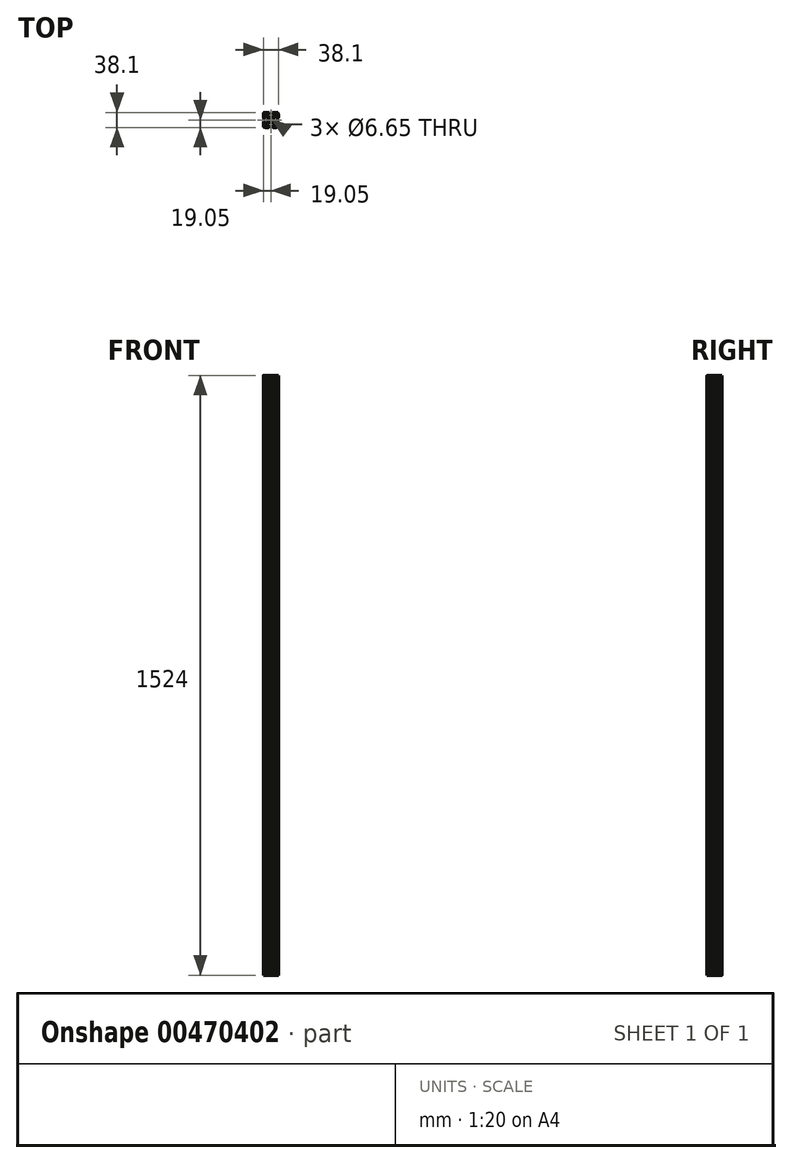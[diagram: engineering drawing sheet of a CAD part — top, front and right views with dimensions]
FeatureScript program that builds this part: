
annotation { "Feature Type Name" : "Feature", "Feature Type Description" : "" }
export const myFeature = defineFeature(function(context is Context, id is Id, definition is map)
    precondition{}
    {
        {
            var Q0;
            Q0=qCreatedBy(makeId("Top.planeOp"),FACE);
            var sketch = newSketch(context, id + "F0", { "sketchPlane" : qUnion([Q0])});
            skCircle(sketch, "E0", {"center": v(0, 0) * mm, "radius": 3.33 * mm});
            skArc(sketch, "E1", {"start": v(-10.29, 13.55) * mm, "mid": v(-10.22, 13.2) * mm, "end": v(-10.02, 12.91) * mm});
            skLineSegment(sketch, "E2", {"start": v(-10.29, 13.55) * mm, "end": v(-10.29, 14.08) * mm});
            skArc(sketch, "E3", {"start": v(-9.39, 14.99) * mm, "mid": v(-10.02, 14.72) * mm, "end": v(-10.29, 14.08) * mm});
            skLineSegment(sketch, "E4", {"start": v(-9.39, 14.99) * mm, "end": v(-5.62, 14.99) * mm});
            skArc(sketch, "E5", {"start": v(-5.62, 14.99) * mm, "mid": v(-4.52, 15.44) * mm, "end": v(-4.06, 16.54) * mm});
            skLineSegment(sketch, "E6", {"start": v(-4.06, 16.54) * mm, "end": v(-4.06, 17.5) * mm});
            skArc(sketch, "E7", {"start": v(-4.06, 17.5) * mm, "mid": v(-4.52, 18.6) * mm, "end": v(-5.62, 19.05) * mm});
            skLineSegment(sketch, "E8", {"start": v(-5.62, 19.05) * mm, "end": v(-7.97, 19.05) * mm});
            skArc(sketch, "E9", {"start": v(-9.5, 19.05) * mm, "mid": v(-8.74, 18.29) * mm, "end": v(-7.97, 19.05) * mm});
            skLineSegment(sketch, "E10", {"start": v(-9.5, 19.05) * mm, "end": v(-14.33, 19.05) * mm});
            skArc(sketch, "E11", {"start": v(-15.85, 19.05) * mm, "mid": v(-15.09, 18.23) * mm, "end": v(-14.33, 19.05) * mm});
            skArc(sketch, "E12", {"start": v(-15.85, 19.05) * mm, "mid": v(-18.12, 18.12) * mm, "end": v(-19.05, 15.85) * mm});
            skArc(sketch, "E13", {"start": v(-19.05, 14.33) * mm, "mid": v(-18.23, 15.09) * mm, "end": v(-19.05, 15.85) * mm});
            skLineSegment(sketch, "E14", {"start": v(-19.05, 14.33) * mm, "end": v(-19.05, 9.5) * mm});
            skArc(sketch, "E15", {"start": v(-19.05, 7.98) * mm, "mid": v(-18.23, 8.74) * mm, "end": v(-19.05, 9.5) * mm});
            skLineSegment(sketch, "E16", {"start": v(-19.05, 7.98) * mm, "end": v(-19.05, 5.62) * mm});
            skArc(sketch, "E17", {"start": v(-19.05, 5.62) * mm, "mid": v(-18.6, 4.52) * mm, "end": v(-17.5, 4.06) * mm});
            skLineSegment(sketch, "E18", {"start": v(-17.5, 4.06) * mm, "end": v(-16.54, 4.06) * mm});
            skArc(sketch, "E19", {"start": v(-16.54, 4.06) * mm, "mid": v(-15.44, 4.52) * mm, "end": v(-14.99, 5.62) * mm});
            skLineSegment(sketch, "E20", {"start": v(-14.99, 5.62) * mm, "end": v(-14.99, 9.39) * mm});
            skArc(sketch, "E21", {"start": v(-14.08, 10.29) * mm, "mid": v(-14.72, 10.02) * mm, "end": v(-14.99, 9.39) * mm});
            skLineSegment(sketch, "E22", {"start": v(-14.08, 10.29) * mm, "end": v(-13.52, 10.29) * mm});
            skArc(sketch, "E23", {"start": v(-12.88, 10.02) * mm, "mid": v(-13.17, 10.22) * mm, "end": v(-13.52, 10.29) * mm});
            skLineSegment(sketch, "E24", {"start": v(-12.88, 10.02) * mm, "end": v(-8.15, 5.3) * mm});
            skArc(sketch, "E25", {"start": v(-6.76, 1.93) * mm, "mid": v(-7.12, 3.75) * mm, "end": v(-8.15, 5.3) * mm});
            skLineSegment(sketch, "E26", {"start": v(-6.76, 1.93) * mm, "end": v(-6.76, -1.93) * mm});
            skArc(sketch, "E27", {"start": v(-8.15, -5.3) * mm, "mid": v(-7.12, -3.75) * mm, "end": v(-6.76, -1.93) * mm});
            skLineSegment(sketch, "E28", {"start": v(-8.15, -5.3) * mm, "end": v(-12.88, -10.02) * mm});
            skArc(sketch, "E29", {"start": v(-13.52, -10.29) * mm, "mid": v(-13.17, -10.22) * mm, "end": v(-12.88, -10.02) * mm});
            skLineSegment(sketch, "E30", {"start": v(-13.52, -10.29) * mm, "end": v(-14.08, -10.29) * mm});
            skArc(sketch, "E31", {"start": v(-14.99, -9.39) * mm, "mid": v(-14.72, -10.02) * mm, "end": v(-14.08, -10.29) * mm});
            skLineSegment(sketch, "E32", {"start": v(-14.99, -9.39) * mm, "end": v(-14.99, -5.62) * mm});
            skArc(sketch, "E33", {"start": v(-14.99, -5.62) * mm, "mid": v(-15.44, -4.52) * mm, "end": v(-16.54, -4.06) * mm});
            skLineSegment(sketch, "E34", {"start": v(-16.54, -4.06) * mm, "end": v(-17.5, -4.06) * mm});
            skArc(sketch, "E35", {"start": v(-17.5, -4.06) * mm, "mid": v(-18.6, -4.52) * mm, "end": v(-19.05, -5.62) * mm});
            skLineSegment(sketch, "E36", {"start": v(-19.05, -5.62) * mm, "end": v(-19.05, -7.98) * mm});
            skArc(sketch, "E37", {"start": v(-19.05, -9.5) * mm, "mid": v(-18.23, -8.74) * mm, "end": v(-19.05, -7.98) * mm});
            skLineSegment(sketch, "E38", {"start": v(-19.05, -9.5) * mm, "end": v(-19.05, -14.33) * mm});
            skArc(sketch, "E39", {"start": v(-19.05, -15.85) * mm, "mid": v(-18.23, -15.09) * mm, "end": v(-19.05, -14.33) * mm});
            skArc(sketch, "E40", {"start": v(-19.05, -15.85) * mm, "mid": v(-18.12, -18.12) * mm, "end": v(-15.85, -19.05) * mm});
            skArc(sketch, "E41", {"start": v(-14.33, -19.05) * mm, "mid": v(-15.09, -18.23) * mm, "end": v(-15.85, -19.05) * mm});
            skLineSegment(sketch, "E42", {"start": v(-14.33, -19.05) * mm, "end": v(-9.5, -19.05) * mm});
            skArc(sketch, "E43", {"start": v(-7.98, -19.05) * mm, "mid": v(-8.74, -18.23) * mm, "end": v(-9.5, -19.05) * mm});
            skLineSegment(sketch, "E44", {"start": v(-7.98, -19.05) * mm, "end": v(-5.62, -19.05) * mm});
            skArc(sketch, "E45", {"start": v(-5.62, -19.05) * mm, "mid": v(-4.52, -18.6) * mm, "end": v(-4.06, -17.5) * mm});
            skLineSegment(sketch, "E46", {"start": v(-4.06, -17.5) * mm, "end": v(-4.06, -16.54) * mm});
            skArc(sketch, "E47", {"start": v(-4.06, -16.54) * mm, "mid": v(-4.52, -15.44) * mm, "end": v(-5.62, -14.99) * mm});
            skLineSegment(sketch, "E48", {"start": v(-5.62, -14.99) * mm, "end": v(-9.39, -14.99) * mm});
            skArc(sketch, "E49", {"start": v(-10.29, -14.08) * mm, "mid": v(-10.02, -14.72) * mm, "end": v(-9.39, -14.99) * mm});
            skLineSegment(sketch, "E50", {"start": v(-10.29, -14.08) * mm, "end": v(-10.29, -13.55) * mm});
            skArc(sketch, "E51", {"start": v(-10.02, -12.91) * mm, "mid": v(-10.22, -13.2) * mm, "end": v(-10.29, -13.55) * mm});
            skLineSegment(sketch, "E52", {"start": v(-10.02, -12.91) * mm, "end": v(-5.25, -8.14) * mm});
            skArc(sketch, "E53", {"start": v(-1.9, -6.76) * mm, "mid": v(-3.72, -7.12) * mm, "end": v(-5.25, -8.14) * mm});
            skLineSegment(sketch, "E54", {"start": v(-1.9, -6.76) * mm, "end": v(1.9, -6.76) * mm});
            skArc(sketch, "E55", {"start": v(5.25, -8.14) * mm, "mid": v(3.72, -7.12) * mm, "end": v(1.9, -6.76) * mm});
            skLineSegment(sketch, "E56", {"start": v(5.25, -8.14) * mm, "end": v(10.02, -12.91) * mm});
            skArc(sketch, "E57", {"start": v(10.29, -13.55) * mm, "mid": v(10.22, -13.2) * mm, "end": v(10.02, -12.91) * mm});
            skLineSegment(sketch, "E58", {"start": v(10.29, -13.55) * mm, "end": v(10.29, -14.08) * mm});
            skArc(sketch, "E59", {"start": v(9.39, -14.99) * mm, "mid": v(10.02, -14.72) * mm, "end": v(10.29, -14.08) * mm});
            skLineSegment(sketch, "E60", {"start": v(9.39, -14.99) * mm, "end": v(5.62, -14.99) * mm});
            skArc(sketch, "E61", {"start": v(5.62, -14.99) * mm, "mid": v(4.52, -15.44) * mm, "end": v(4.06, -16.54) * mm});
            skLineSegment(sketch, "E62", {"start": v(4.06, -16.54) * mm, "end": v(4.06, -17.5) * mm});
            skArc(sketch, "E63", {"start": v(4.06, -17.5) * mm, "mid": v(4.52, -18.6) * mm, "end": v(5.62, -19.05) * mm});
            skLineSegment(sketch, "E64", {"start": v(5.62, -19.05) * mm, "end": v(7.98, -19.05) * mm});
            skArc(sketch, "E65", {"start": v(9.5, -19.05) * mm, "mid": v(8.74, -18.23) * mm, "end": v(7.98, -19.05) * mm});
            skLineSegment(sketch, "E66", {"start": v(9.5, -19.05) * mm, "end": v(14.33, -19.05) * mm});
            skArc(sketch, "E67", {"start": v(15.85, -19.05) * mm, "mid": v(15.09, -18.23) * mm, "end": v(14.33, -19.05) * mm});
            skArc(sketch, "E68", {"start": v(15.85, -19.05) * mm, "mid": v(18.12, -18.12) * mm, "end": v(19.05, -15.85) * mm});
            skArc(sketch, "E69", {"start": v(19.05, -14.33) * mm, "mid": v(18.23, -15.09) * mm, "end": v(19.05, -15.85) * mm});
            skLineSegment(sketch, "E70", {"start": v(19.05, -14.33) * mm, "end": v(19.05, -9.5) * mm});
            skArc(sketch, "E71", {"start": v(19.05, -7.98) * mm, "mid": v(18.23, -8.74) * mm, "end": v(19.05, -9.5) * mm});
            skLineSegment(sketch, "E72", {"start": v(19.05, -7.98) * mm, "end": v(19.05, -5.62) * mm});
            skArc(sketch, "E73", {"start": v(19.05, -5.62) * mm, "mid": v(18.6, -4.52) * mm, "end": v(17.5, -4.06) * mm});
            skLineSegment(sketch, "E74", {"start": v(17.5, -4.06) * mm, "end": v(16.54, -4.06) * mm});
            skArc(sketch, "E75", {"start": v(16.54, -4.06) * mm, "mid": v(15.44, -4.52) * mm, "end": v(14.99, -5.62) * mm});
            skLineSegment(sketch, "E76", {"start": v(14.99, -5.62) * mm, "end": v(14.99, -9.39) * mm});
            skArc(sketch, "E77", {"start": v(14.08, -10.29) * mm, "mid": v(14.72, -10.02) * mm, "end": v(14.99, -9.39) * mm});
            skLineSegment(sketch, "E78", {"start": v(14.08, -10.29) * mm, "end": v(13.52, -10.29) * mm});
            skArc(sketch, "E79", {"start": v(12.88, -10.02) * mm, "mid": v(13.17, -10.22) * mm, "end": v(13.52, -10.29) * mm});
            skLineSegment(sketch, "E80", {"start": v(12.88, -10.02) * mm, "end": v(8.15, -5.3) * mm});
            skArc(sketch, "E81", {"start": v(6.76, -1.93) * mm, "mid": v(7.12, -3.75) * mm, "end": v(8.15, -5.3) * mm});
            skLineSegment(sketch, "E82", {"start": v(6.76, -1.93) * mm, "end": v(6.76, 1.93) * mm});
            skArc(sketch, "E83", {"start": v(8.15, 5.3) * mm, "mid": v(7.12, 3.75) * mm, "end": v(6.76, 1.93) * mm});
            skLineSegment(sketch, "E84", {"start": v(8.15, 5.3) * mm, "end": v(12.88, 10.02) * mm});
            skArc(sketch, "E85", {"start": v(13.52, 10.29) * mm, "mid": v(13.17, 10.22) * mm, "end": v(12.88, 10.02) * mm});
            skLineSegment(sketch, "E86", {"start": v(13.52, 10.29) * mm, "end": v(14.08, 10.29) * mm});
            skArc(sketch, "E87", {"start": v(14.99, 9.39) * mm, "mid": v(14.72, 10.02) * mm, "end": v(14.08, 10.29) * mm});
            skLineSegment(sketch, "E88", {"start": v(14.99, 9.39) * mm, "end": v(14.99, 5.62) * mm});
            skArc(sketch, "E89", {"start": v(14.99, 5.62) * mm, "mid": v(15.44, 4.52) * mm, "end": v(16.54, 4.06) * mm});
            skLineSegment(sketch, "E90", {"start": v(16.54, 4.06) * mm, "end": v(17.5, 4.06) * mm});
            skArc(sketch, "E91", {"start": v(17.5, 4.06) * mm, "mid": v(18.6, 4.52) * mm, "end": v(19.05, 5.62) * mm});
            skLineSegment(sketch, "E92", {"start": v(19.05, 5.62) * mm, "end": v(19.05, 7.98) * mm});
            skArc(sketch, "E93", {"start": v(19.05, 9.5) * mm, "mid": v(18.23, 8.74) * mm, "end": v(19.05, 7.98) * mm});
            skLineSegment(sketch, "E94", {"start": v(19.05, 9.5) * mm, "end": v(19.05, 14.33) * mm});
            skArc(sketch, "E95", {"start": v(19.05, 15.85) * mm, "mid": v(18.23, 15.09) * mm, "end": v(19.05, 14.33) * mm});
            skArc(sketch, "E96", {"start": v(19.05, 15.85) * mm, "mid": v(18.12, 18.12) * mm, "end": v(15.85, 19.05) * mm});
            skArc(sketch, "E97", {"start": v(14.33, 19.05) * mm, "mid": v(15.09, 18.23) * mm, "end": v(15.85, 19.05) * mm});
            skLineSegment(sketch, "E98", {"start": v(14.33, 19.05) * mm, "end": v(9.5, 19.05) * mm});
            skArc(sketch, "E99", {"start": v(7.97, 19.05) * mm, "mid": v(8.74, 18.29) * mm, "end": v(9.5, 19.05) * mm});
            skLineSegment(sketch, "E100", {"start": v(7.97, 19.05) * mm, "end": v(5.62, 19.05) * mm});
            skArc(sketch, "E101", {"start": v(5.62, 19.05) * mm, "mid": v(4.52, 18.6) * mm, "end": v(4.06, 17.5) * mm});
            skLineSegment(sketch, "E102", {"start": v(4.06, 17.5) * mm, "end": v(4.06, 16.54) * mm});
            skArc(sketch, "E103", {"start": v(4.06, 16.54) * mm, "mid": v(4.52, 15.44) * mm, "end": v(5.62, 14.99) * mm});
            skLineSegment(sketch, "E104", {"start": v(5.62, 14.99) * mm, "end": v(9.39, 14.99) * mm});
            skArc(sketch, "E105", {"start": v(10.29, 14.08) * mm, "mid": v(10.02, 14.72) * mm, "end": v(9.39, 14.99) * mm});
            skLineSegment(sketch, "E106", {"start": v(10.29, 14.08) * mm, "end": v(10.29, 13.55) * mm});
            skArc(sketch, "E107", {"start": v(10.02, 12.91) * mm, "mid": v(10.22, 13.2) * mm, "end": v(10.29, 13.55) * mm});
            skLineSegment(sketch, "E108", {"start": v(10.02, 12.91) * mm, "end": v(5.25, 8.14) * mm});
            skArc(sketch, "E109", {"start": v(1.9, 6.76) * mm, "mid": v(3.72, 7.12) * mm, "end": v(5.25, 8.14) * mm});
            skLineSegment(sketch, "E110", {"start": v(1.9, 6.76) * mm, "end": v(-1.9, 6.76) * mm});
            skArc(sketch, "E111", {"start": v(-5.25, 8.14) * mm, "mid": v(-3.72, 7.12) * mm, "end": v(-1.9, 6.76) * mm});
            skLineSegment(sketch, "E112", {"start": v(-5.25, 8.14) * mm, "end": v(-10.02, 12.91) * mm});
            skSolve(sketch);
        }
        {
            var Q0;
            Q0 = qSketchRegion(id + "F0", true);
            extrude(context, id + "F1", {"entities" : qUnion([Q0]), "depth" : 588.96 * mm});
        }
        {
            var Q0;
            Q0 = qSketchRegion(id + "F0", true);
            extrude(context, id + "F2", {"entities" : qUnion([Q0]), "depth" : 838.2 * mm});
        }
        {
            var Q0;
            Q0 = qSketchRegion(id + "F0", true);
            extrude(context, id + "F3", {"entities" : qUnion([Q0]), "depth" : 1524 * mm});
        }
    });
